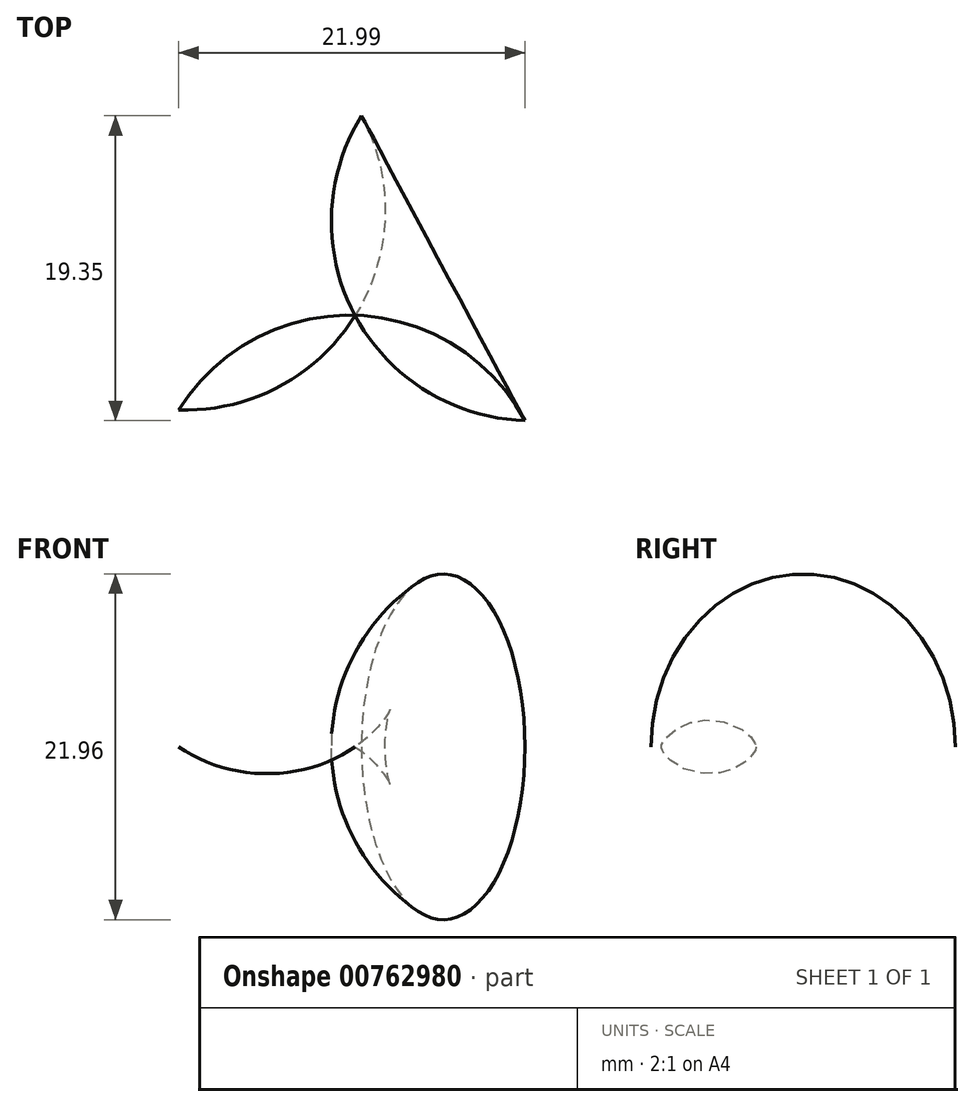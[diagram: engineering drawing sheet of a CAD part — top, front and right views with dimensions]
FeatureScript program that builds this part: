
annotation { "Feature Type Name" : "Feature", "Feature Type Description" : "" }
export const myFeature = defineFeature(function(context is Context, id is Id, definition is map)
    precondition{}
    {
        {
            var Q0;
            Q0=qCreatedBy(makeId("Top.planeOp"),FACE);
            var sketch = newSketch(context, id + "F0", { "sketchPlane" : qUnion([Q0])});
            skPoint(sketch, "E0.0.midPoint", {"position": v(-11.4, -6.11) * mm});
            skArc(sketch, "E1", {"start": v(-0.2, -0.12) * mm, "mid": v(-6.6, -1.62) * mm, "end": v(-11.4, -6.11) * mm});
            skArc(sketch, "E2", {"start": v(0.2, 12.57) * mm, "mid": v(-1.7, 6.28) * mm, "end": v(-0.2, -0.12) * mm});
            skArc(sketch, "E3", {"start": v(-0.2, -0.12) * mm, "mid": v(1.7, 6.17) * mm, "end": v(0.2, 12.57) * mm});
            skPoint(sketch, "E4.orphan", {"position": v(16.16, -15.71) * mm});
            skPoint(sketch, "E5.orphan", {"position": v(-1.02, -25.5) * mm});
            skPoint(sketch, "E0.1.end.orphan", {"position": v(8.89, -59.1) * mm});
            skLineSegment(sketch, "E6", {"start": v(-11.4, -6.11) * mm, "end": v(0, 0) * mm});
            skSolve(sketch);
        }
        {
            var Q0;
            {var subQ0=sQuery(id+"F0.wireOp",EDGE,"E6");var subQ1=sQuery(id+"F0.wireOp",EDGE,"E1");var subQ2=makeQuery(id+"F0.imprint","INTERSECT",VERTEX,{"disambiguationData":[OD(0.0)],"derivedFrom":[subQ1,subQ0]});Q0=makeQuery(id+"F0.imprint","IMPRINT",FACE,{"disambiguationData":[TD([[makeQuery(id+"F0.imprint","IMPRINT",EDGE,{"disambiguationData":[TD([[subQ2,1.0]])],"derivedFrom":subQ1}),1.0]])]});}
            var Q1;
            {var subQ0=sQuery(id+"F0.wireOp",EDGE,"E3");var subQ1=sQuery(id+"F0.wireOp",EDGE,"E2");var subQ2=makeQuery(id+"F0.imprint","INTERSECT",VERTEX,{"derivedFrom":[subQ1,subQ0]});Q1=makeQuery(id+"F0.imprint","IMPRINT",FACE,{"disambiguationData":[TD([[makeQuery(id+"F0.imprint","IMPRINT",EDGE,{"disambiguationData":[TD([[subQ2,-1.0]])],"derivedFrom":subQ1}),1.0]])]});}
            var Q2;
            Q2=sQuery(id+"F0.wireOp",EDGE,"E6");
            revolve(context, id + "F1", {"surfaceOperationType" : NewSurfaceOperationType.NEW, "entities" : qUnion([Q0, Q1]), "axis" : qUnion([Q2]), "revolveType" : RevolveType.FULL});
        }
    });
